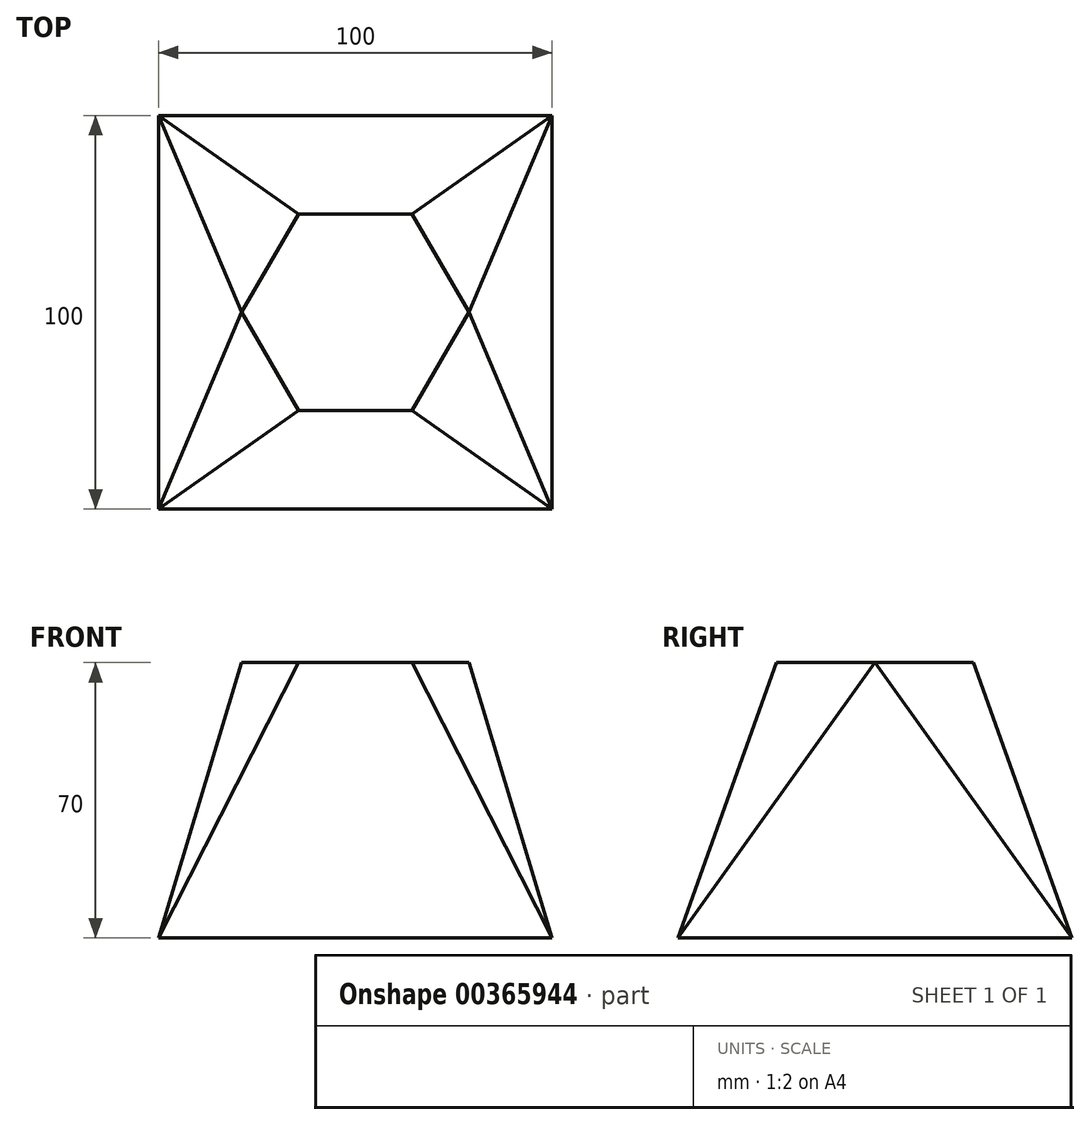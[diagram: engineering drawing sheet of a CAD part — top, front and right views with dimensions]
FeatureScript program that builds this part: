
annotation { "Feature Type Name" : "Feature", "Feature Type Description" : "" }
export const myFeature = defineFeature(function(context is Context, id is Id, definition is map)
    precondition{}
    {
        {
            var Q0;
            Q0=qCreatedBy(makeId("Top.planeOp"),FACE);
            var sketch = newSketch(context, id + "F0", { "sketchPlane" : qUnion([Q0])});
            skLineSegment(sketch, "E0.bottom", {"start": v(-50, 50) * mm, "end": v(50, 50) * mm});
            skLineSegment(sketch, "E0.top", {"start": v(-50, -50) * mm, "end": v(50, -50) * mm});
            skLineSegment(sketch, "E0.left", {"start": v(-50, 50) * mm, "end": v(-50, -50) * mm});
            skLineSegment(sketch, "E0.right", {"start": v(50, 50) * mm, "end": v(50, -50) * mm});
            skSolve(sketch);
        }
        {
            var Q0;
            Q0=qCreatedBy(makeId("Top.planeOp"),FACE);
            cPlane(context, id + "F1", {"entities" : qUnion([Q0]), "cplaneType" : CPlaneType.OFFSET, "offset" : 70 * mm, "width" : 150 * mm, "height" : 150 * mm});
        }
        {
            var Q0;
            Q0=qCreatedBy(id+"F1.planeOp",FACE);
            var sketch = newSketch(context, id + "F2", { "sketchPlane" : qUnion([Q0])});
            skCircle(sketch, "E1.cCircle", {"center": v(0, 0) * mm, "radius": 25 * mm, "construction": true});
            skLineSegment(sketch, "E1.0", {"start": v(-14.43, 25) * mm, "end": v(14.43, 25) * mm});
            skLineSegment(sketch, "E1.1", {"start": v(14.43, 25) * mm, "end": v(28.87, 0) * mm});
            skLineSegment(sketch, "E1.2", {"start": v(28.87, 0) * mm, "end": v(14.43, -25) * mm});
            skLineSegment(sketch, "E1.3", {"start": v(14.43, -25) * mm, "end": v(-14.43, -25) * mm});
            skLineSegment(sketch, "E1.4", {"start": v(-14.43, -25) * mm, "end": v(-28.87, 0) * mm});
            skLineSegment(sketch, "E1.5", {"start": v(-28.87, 0) * mm, "end": v(-14.43, 25) * mm});
            skPoint(sketch, "E1.0.midPoint", {"position": v(0, 25) * mm});
            skLineSegment(sketch, "E2", {"start": v(-14.43, 25) * mm, "end": v(-14.43, -25) * mm});
            skLineSegment(sketch, "E3", {"start": v(14.43, 25) * mm, "end": v(14.43, -25) * mm});
            skSolve(sketch);
        }
        {
            var Q0;
            Q0=makeQuery(id+"F2.imprint","IMPRINT",FACE,{"disambiguationData":[TD([[makeQuery(id+"F2.imprint","IMPRINT",EDGE,{"derivedFrom":sQuery(id+"F2.wireOp",EDGE,"E1.0")}),-1.0]])]});
            var Q1;
            Q1=makeQuery(id+"F0.imprint","IMPRINT",FACE,{"disambiguationData":[TD([[makeQuery(id+"F0.imprint","IMPRINT",EDGE,{"derivedFrom":sQuery(id+"F0.wireOp",EDGE,"E0.bottom")}),-1.0]])]});
            loft(context, id + "F3", {"sheetProfilesArray" : [{ "sheetProfileEntities" : qUnion([Q0]) }, { "sheetProfileEntities" : qUnion([Q1]) }]});
        }
        {
            var Q1;
            Q1=sQuery(id+"F2.wireOp",VERTEX,"E1.5.start");
            var Q2;
            Q2=makeQuery(id+"F3.opLoft","SWEPT_FACE",FACE,{"disambiguationData":[OSD([sQuery(id+"F0.wireOp",EDGE,"E0.bottom"),sQuery(id+"F0.wireOp",EDGE,"E0.top"),sQuery(id+"F0.wireOp",EDGE,"E0.left"),sQuery(id+"F2.wireOp",EDGE,"E1.0"),sQuery(id+"F2.wireOp",EDGE,"E1.3"),sQuery(id+"F2.wireOp",EDGE,"E1.4"),sQuery(id+"F2.wireOp",EDGE,"E1.5"),sQuery(id+"F2.wireOp",EDGE,"E2")])]});
            loft(context, id + "F4", {"operationType" : NewBodyOperationType.ADD, "sheetProfilesArray" : [{ "sheetProfileEntities" : qUnion([Q1]) }, { "sheetProfileEntities" : qUnion([Q2]) }]});
        }
        {
            var Q1;
            Q1=sQuery(id+"F2.wireOp",VERTEX,"E1.2.start");
            var Q2;
            Q2=makeQuery(id+"F3.opLoft","SWEPT_FACE",FACE,{"disambiguationData":[OSD([sQuery(id+"F0.wireOp",EDGE,"E0.bottom"),sQuery(id+"F0.wireOp",EDGE,"E0.top"),sQuery(id+"F0.wireOp",EDGE,"E0.right"),sQuery(id+"F2.wireOp",EDGE,"E1.0"),sQuery(id+"F2.wireOp",EDGE,"E1.1"),sQuery(id+"F2.wireOp",EDGE,"E1.2"),sQuery(id+"F2.wireOp",EDGE,"E1.3"),sQuery(id+"F2.wireOp",EDGE,"E3")])]});
            loft(context, id + "F5", {"operationType" : NewBodyOperationType.ADD, "sheetProfilesArray" : [{ "sheetProfileEntities" : qUnion([Q1]) }, { "sheetProfileEntities" : qUnion([Q2]) }]});
        }
    });
